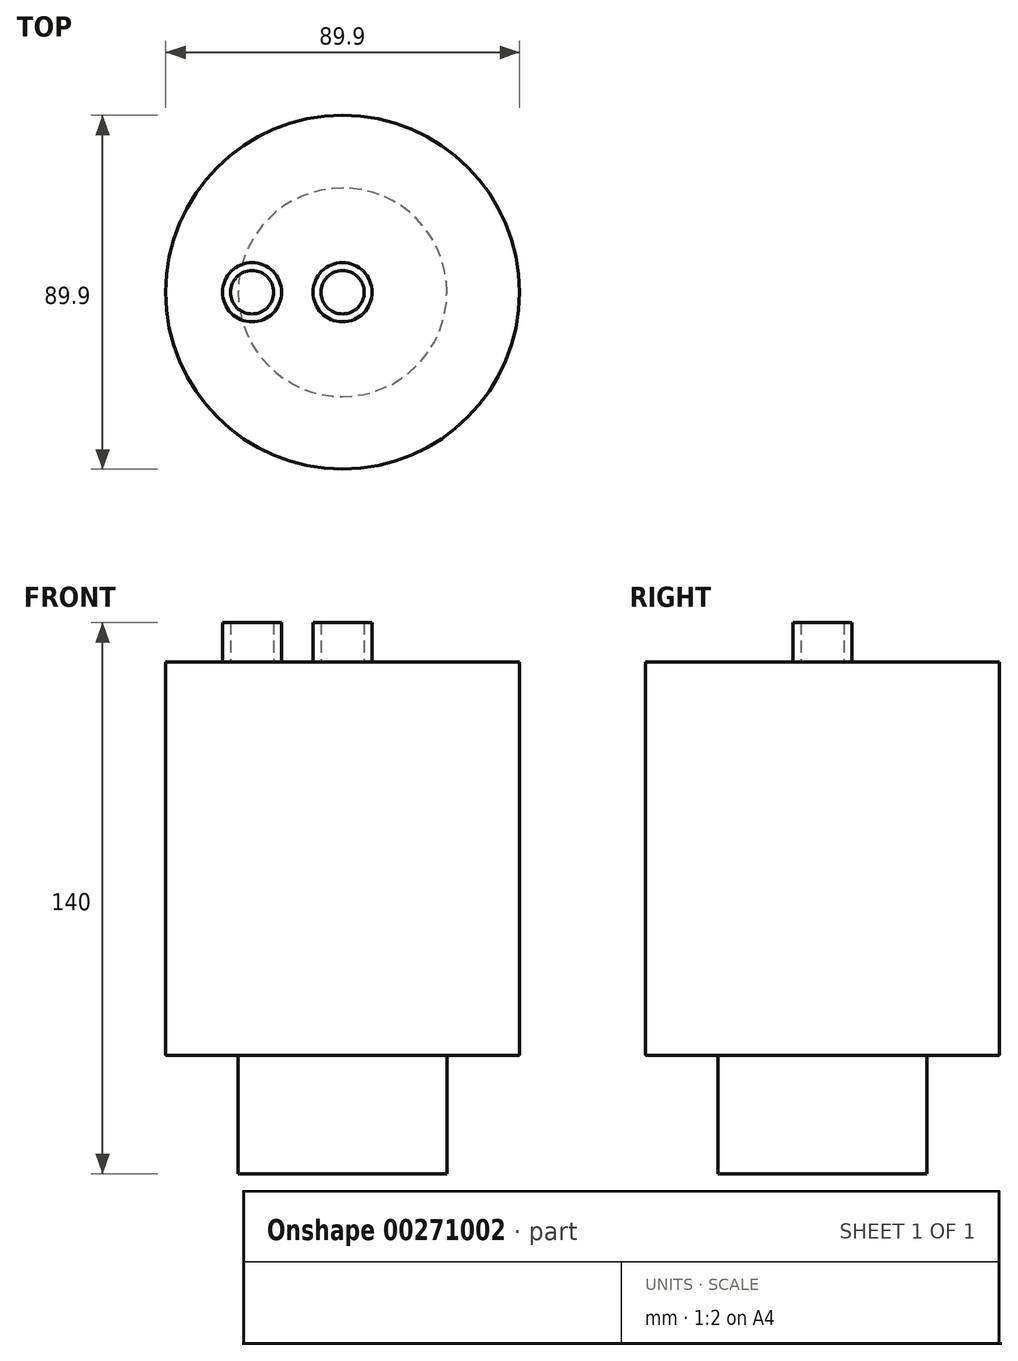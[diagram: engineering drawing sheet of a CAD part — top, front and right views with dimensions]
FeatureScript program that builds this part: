
annotation { "Feature Type Name" : "Feature", "Feature Type Description" : "" }
export const myFeature = defineFeature(function(context is Context, id is Id, definition is map)
    precondition{}
    {
        {
            var Q0;
            Q0=qCreatedBy(makeId("Top.planeOp"),FACE);
            var sketch = newSketch(context, id + "F0", { "sketchPlane" : qUnion([Q0])});
            skCircle(sketch, "E0", {"center": v(0, 0) * mm, "radius": 44.95 * mm});
            skSolve(sketch);
        }
        {
            var Q0;
            Q0=makeQuery(id+"F0.imprint","IMPRINT",FACE,{"disambiguationData":[TD([[makeQuery(id+"F0.imprint","IMPRINT",EDGE,{"derivedFrom":sQuery(id+"F0.wireOp",EDGE,"E0")}),1.0]])]});
            var Q1;
            Q1=sQuery(id+"F0.wireOp",EDGE,"E0");
            extrude(context, id + "F1", {"entities" : qUnion([Q0]), "surfaceEntities" : qUnion([Q1]), "depth" : 130 * mm});
        }
        {
            var Q0;
            Q0=makeQuery(id+"F1.opExtrude","CAP_FACE",FACE,{"disambiguationData":[OSD([sQuery(id+"F0.wireOp",EDGE,"E0")])],"isStart":false});
            var sketch = newSketch(context, id + "F2", { "sketchPlane" : qUnion([Q0])});
            skCircle(sketch, "E1", {"center": v(-23, 0) * mm, "radius": 7.5 * mm});
            skCircle(sketch, "E2", {"center": v(0, 0) * mm, "radius": 7.5 * mm});
            skCircle(sketch, "E3", {"center": v(-23, 0) * mm, "radius": 5.5 * mm});
            skCircle(sketch, "E4", {"center": v(0, 0) * mm, "radius": 5.5 * mm});
            skSolve(sketch);
        }
        {
            var Q0;
            Q0=makeQuery(id+"F2.imprint","IMPRINT",FACE,{"disambiguationData":[TD([[makeQuery(id+"F2.imprint","IMPRINT",EDGE,{"derivedFrom":sQuery(id+"F2.wireOp",EDGE,"E2")}),1.0]])]});
            var Q1;
            Q1=makeQuery(id+"F2.imprint","IMPRINT",FACE,{"disambiguationData":[TD([[makeQuery(id+"F2.imprint","IMPRINT",EDGE,{"derivedFrom":sQuery(id+"F2.wireOp",EDGE,"E1")}),1.0]])]});
            extrude(context, id + "F3", {"entities" : qUnion([Q0, Q1]), "operationType" : NewBodyOperationType.ADD, "depth" : 10 * mm});
        }
        {
            var Q0;
            Q0=makeQuery(id+"F1.opExtrude","CAP_FACE",FACE,{"disambiguationData":[OSD([sQuery(id+"F0.wireOp",EDGE,"E0")])],"isStart":true});
            var sketch = newSketch(context, id + "F4", { "sketchPlane" : qUnion([Q0])});
            skCircle(sketch, "E5", {"center": v(0, 0) * mm, "radius": 26.5 * mm});
            skCircle(sketch, "E6", {"center": v(0, 0) * mm, "radius": 45 * mm});
            skSolve(sketch);
        }
        {
            var Q0;
            Q0=makeQuery(id+"F4.imprint","IMPRINT",FACE,{"disambiguationData":[TD([[makeQuery(id+"F4.imprint","IMPRINT",EDGE,{"derivedFrom":sQuery(id+"F4.wireOp",EDGE,"E5")}),-1.0]])]});
            extrude(context, id + "F5", {"entities" : qUnion([Q0]), "operationType" : NewBodyOperationType.REMOVE, "oppositeDirection" : true, "depth" : 30 * mm});
        }
    });
